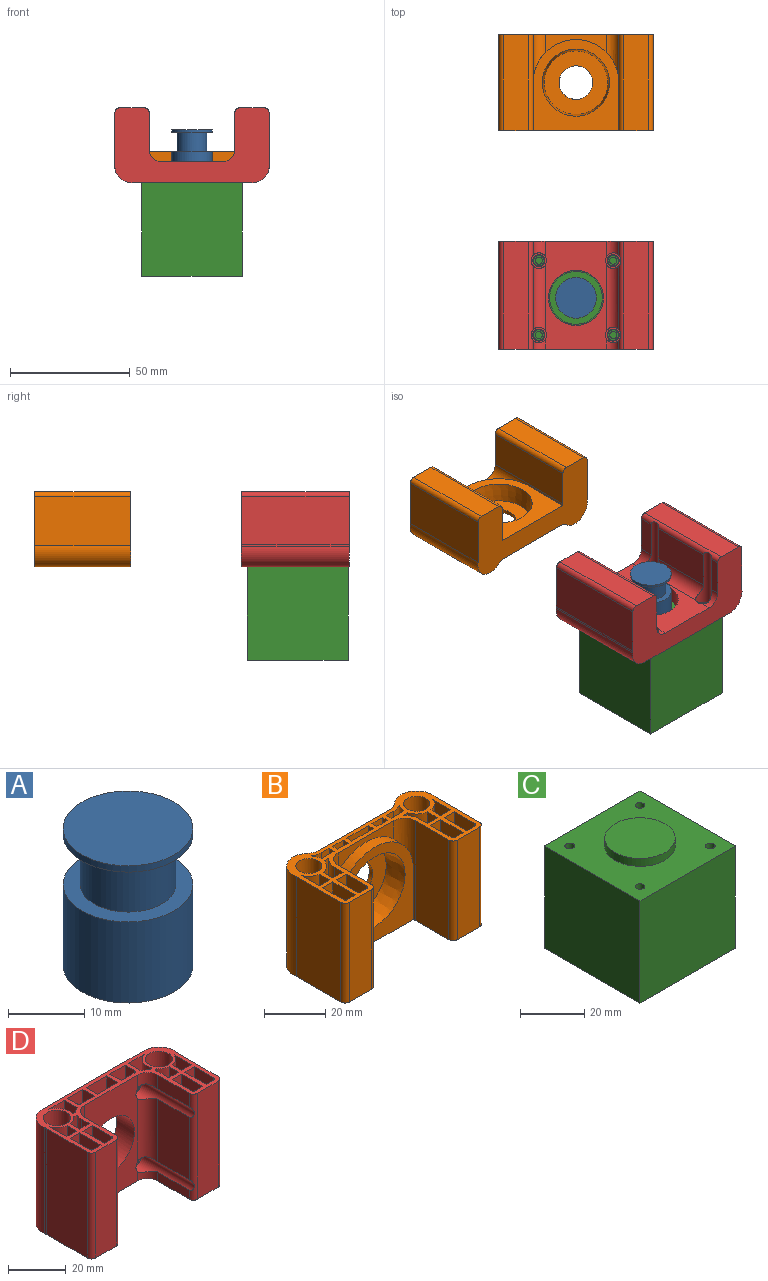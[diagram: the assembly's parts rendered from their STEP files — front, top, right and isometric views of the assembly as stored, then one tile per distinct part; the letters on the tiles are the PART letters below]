
ASSEMBLY  parts=4 mates=6
PART A: 7 faces, bbox 17x17x22 mm
  f0: cylinder r=6.25mm len=12.5mm, axis (0,0,1), area 314.2mm2, adj f3,f5
  f1: cylinder r=8.5mm len=17mm, axis (0,0,-1), area 694.3mm2, adj f2,f3
  f2: plane 17x17mm, normal (0,0,-1), area 227mm2, adj f1
  f3: plane 17x17mm, normal (0,0,1), area 104.3mm2, adj f0,f1
  f4: cylinder r=8.5mm len=17mm, axis (0,0,1), area 53.4mm2, adj f5,f6
  f5: plane 17x17mm, normal (0,0,-1), area 104.3mm2, adj f0,f4
  f6: plane 17x17mm, normal (0,0,1), area 227mm2, adj f4
PART B: 130 faces, bbox 64.5x31.3x40 mm
  f0: plane 10.18x2.3mm, normal (1,0,0), area 23.4mm2, adj f10,f16,f52,f109
  f1: plane 12.46x2.3mm, normal (-1,0,0), area 28.7mm2, adj f11,f52,f78,f106
  f2: plane 5.65x2.3mm, normal (1,0,0), area 13mm2, adj f9,f15,f52,f108
  f3: plane 6.31x2.3mm, normal (-1,0,0), area 14.5mm2, adj f10,f16,f52,f109
  f4: plane 5.65x2.3mm, normal (-1,0,0), area 13mm2, adj f9,f15,f52,f108
  f5: plane 6.31x2.3mm, normal (1,0,0), area 14.5mm2, adj f8,f14,f52,f107
  f6: plane 10.18x2.3mm, normal (-1,0,0), area 23.4mm2, adj f8,f14,f52,f107
  f7: plane 12.46x2.3mm, normal (1,0,0), area 28.7mm2, adj f52,f67,f88,f105
  f8: plane 10.18x5mm, normal (0,-1,0), area 39.8mm2, adj f5,f6,f52,f107
  f9: plane 10x5.65mm, normal (0,-1,0), area 50.8mm2, adj f2,f4,f52,f108
  f10: plane 10.18x5mm, normal (0,-1,0), area 39.8mm2, adj f0,f3,f52,f109
  f11: plane 38.4x3.49mm, normal (0,-1,0), area 113.6mm2, adj f1,f12,f52,f58,f69,f106
  f12: plane 10.86x2.3mm, normal (-1,0,0), area 25mm2, adj f11,f58,f78,f106
  f13: plane 10.86x2.3mm, normal (1,0,0), area 25mm2, adj f29,f67,f88,f105
  f14: plane 10.18x5mm, normal (0,1,0), area 39.8mm2, adj f5,f6,f52,f107
  f15: plane 10x5.65mm, normal (0,1,0), area 50.8mm2, adj f2,f4,f52,f108
  f16: plane 10.18x5mm, normal (0,1,0), area 39.8mm2, adj f0,f3,f52,f109
  f17: plane 8.85x6.3mm, normal (0,0,1), area 30.1mm2, adj f18,f25,f26,f89,f90,f94,f103
  f18: cylinder r=6.6mm len=38.4mm, axis (0,0,1), area 196.7mm2, adj f17,f26,f52,f89,f102,f103
  f19: cylinder r=5mm len=40mm, axis (0,0,-1), area 122.6mm2, adj f45,f46,f52,f53,f100,f101
  f20: cylinder r=5mm len=40mm, axis (0,0,1), area 122.6mm2, adj f46,f47,f52,f53,f100,f101
  f21: cylinder r=6.6mm len=38.4mm, axis (0,0,-1), area 196.7mm2, adj f31,f52,f63,f79,f98,f99
  f22: plane 8.36x4.7mm, normal (0,0,1), area 26.9mm2, adj f28,f30,f91,f93
  f23: plane 10.45x4.7mm, normal (0,0,1), area 48.9mm2, adj f65,f66,f77,f92,f97
  f24: plane 10.45x4.7mm, normal (0,0,1), area 48.9mm2, adj f27,f64,f76,f95,f96
  f25: cylinder r=5.85mm len=38.4mm, axis (0,0,-1), area 263.8mm2, adj f17,f52,f89,f90
  f26: plane 38.4x3.85mm, normal (1,0,0), area 147.8mm2, adj f17,f18,f52,f94
  f27: plane 38.4x3.7mm, normal (0,1,0), area 142.1mm2, adj f24,f52,f76,f96
  f28: plane 38.4x8.36mm, normal (-1,0,0), area 320.9mm2, adj f22,f30,f52,f93
  f29: plane 7.09x3.37mm, normal (0,0,1), area 15mm2, adj f13,f59,f67,f68,f88
  f30: cylinder r=5.85mm len=38.4mm, axis (0,0,-1), area 243.9mm2, adj f22,f28,f52,f91
  f31: plane 8.85x6.3mm, normal (0,0,1), area 30.1mm2, adj f21,f60,f63,f79,f81,f83,f98
  f32: plane 10.45x4.7mm, normal (0,0,1), area 48.9mm2, adj f37,f62,f75,f82,f87
  f33: plane 8.36x4.7mm, normal (0,0,1), area 26.9mm2, adj f34,f61,f80,f84
  f34: cylinder r=5.85mm len=38.4mm, axis (0,0,-1), area 243.9mm2, adj f33,f52,f61,f80
  f35: plane 38.4x9.45mm, normal (1,0,0), area 362.9mm2, adj f38,f52,f74,f85
  f36: plane 38.4x3.7mm, normal (0,1,0), area 142.1mm2, adj f38,f52,f74,f86
  f37: plane 38.4x9.45mm, normal (-1,0,0), area 362.9mm2, adj f32,f52,f75,f82
  f38: plane 10.45x4.7mm, normal (0,0,1), area 48.9mm2, adj f35,f36,f74,f85,f86
  f39: cylinder r=5.85mm len=38.4mm, axis (0,0,-1), area 138.7mm2, adj f52,f58,f69,f78
  f40: cylinder r=4.25mm len=38mm, axis (0,0,-1), area 1014.7mm2, adj f52,f55
  f41: cylinder r=4.25mm len=38mm, axis (0,0,-1), area 1014.7mm2, adj f52,f54
  f42: cylinder r=7.25mm len=40mm, axis (0,0,-1), area 730.8mm2, adj f43,f52,f53,f57
  f43: plane 40x20.53mm, normal (-1,0,0), area 821.3mm2, adj f42,f52,f53,f70
  f44: plane 40x10.2mm, normal (0,-1,0), area 408mm2, adj f52,f53,f70,f71
  f45: plane 40x15.5mm, normal (1,0,0), area 620mm2, adj f19,f52,f53,f71
  f46: plane 25.8x7.59mm, normal (0,-1,0), area 98.1mm2, adj f19,f20,f52,f101
  f47: plane 40x15.5mm, normal (-1,0,0), area 620mm2, adj f20,f52,f53,f72
  f48: plane 40x10.2mm, normal (0,-1,0), area 408mm2, adj f52,f53,f72,f73
  f49: plane 40x20.53mm, normal (1,0,0), area 821.3mm2, adj f50,f52,f53,f73
  f50: cylinder r=7.25mm len=40mm, axis (0,0,-1), area 730.8mm2, adj f49,f52,f53,f56
  f51: plane 40x33.38mm, normal (0,1,0), area 1181.2mm2, adj f52,f53,f56,f57,f110
  f52: plane 64.5x31.25mm, normal (0,0,1), area 554.8mm2, adj f0,f1,f2,f3,f4,f5,f6,f7
  f53: plane 64.5x31.25mm, normal (0,0,-1), area 1190.4mm2, adj f19,f20,f42,f43,f44,f45,f47,f48
  f54: plane 8.5x8.5mm, normal (0,0,1), area 56.7mm2, adj f41
  f55: plane 8.5x8.5mm, normal (0,0,1), area 56.7mm2, adj f40
  f56: cylinder r=5mm len=40mm, axis (0,0,-1), area 149.1mm2, adj f50,f51,f52,f53
  f57: cylinder r=5mm len=40mm, axis (0,0,-1), area 149.1mm2, adj f42,f51,f52,f53
  f58: plane 7.09x3.37mm, normal (0,0,1), area 15mm2, adj f11,f12,f39,f69,f78
  f59: cylinder r=5.85mm len=38.4mm, axis (0,0,-1), area 138.7mm2, adj f29,f52,f68,f88
  f60: cylinder r=5.85mm len=38.4mm, axis (0,0,-1), area 263.8mm2, adj f31,f52,f79,f81
  f61: plane 38.4x8.36mm, normal (1,0,0), area 320.9mm2, adj f33,f34,f52,f84
  f62: plane 38.4x3.7mm, normal (0,1,0), area 142.1mm2, adj f32,f52,f75,f87
  f63: plane 38.4x3.85mm, normal (-1,0,0), area 147.8mm2, adj f21,f31,f52,f83
  f64: plane 38.4x9.45mm, normal (1,0,0), area 362.9mm2, adj f24,f52,f76,f95
  f65: plane 38.4x3.7mm, normal (0,1,0), area 142.1mm2, adj f23,f52,f77,f97
  f66: plane 38.4x9.45mm, normal (-1,0,0), area 362.9mm2, adj f23,f52,f77,f92
  f67: plane 38.4x3.49mm, normal (0,-1,0), area 113.6mm2, adj f7,f13,f29,f52,f68,f105
  f68: cylinder r=6.6mm len=38.4mm, axis (0,0,-1), area 146.2mm2, adj f29,f52,f59,f67
  f69: cylinder r=6.6mm len=38.4mm, axis (0,0,-1), area 146.2mm2, adj f11,f39,f52,f58
  f70: cylinder r=2mm len=40mm, axis (0,0,-1), area 125.7mm2, adj f43,f44,f52,f53
  f71: cylinder r=2mm len=40mm, axis (0,0,1), area 125.7mm2, adj f44,f45,f52,f53
  f72: cylinder r=2mm len=40mm, axis (0,0,-1), area 125.7mm2, adj f47,f48,f52,f53
  f73: cylinder r=2mm len=40mm, axis (0,0,1), area 125.7mm2, adj f48,f49,f52,f53
  f74: cylinder r=1mm len=38.4mm, axis (0,0,1), area 60.3mm2, adj f35,f36,f38,f52
  f75: cylinder r=1mm len=38.4mm, axis (0,0,-1), area 60.3mm2, adj f32,f37,f52,f62
  f76: cylinder r=1mm len=38.4mm, axis (0,0,1), area 60.3mm2, adj f24,f27,f52,f64
  f77: cylinder r=1mm len=38.4mm, axis (0,0,-1), area 60.3mm2, adj f23,f52,f65,f66
  f78: plane 38.4x5.95mm, normal (0,1,0), area 208.1mm2, adj f1,f12,f39,f52,f58,f106
  f79: plane 38.4x2.14mm, normal (0,-1,0), area 67.1mm2, adj f21,f31,f52,f60,f98,f99
  f80: plane 38.4x4.56mm, normal (-1,0,0), area 174.9mm2, adj f33,f34,f52,f84
  f81: plane 38.4x4.56mm, normal (1,0,0), area 174.9mm2, adj f31,f52,f60,f83
  f82: plane 38.4x4.7mm, normal (0,-1,0), area 180.5mm2, adj f32,f37,f52,f87
  f83: plane 38.4x4.7mm, normal (0,1,0), area 180.5mm2, adj f31,f52,f63,f81
  f84: plane 38.4x4.7mm, normal (0,1,0), area 180.5mm2, adj f33,f52,f61,f80
  f85: plane 38.4x4.7mm, normal (0,-1,0), area 180.5mm2, adj f35,f38,f52,f86
  f86: plane 38.4x10.45mm, normal (-1,0,0), area 401.3mm2, adj f36,f38,f52,f85
  f87: plane 38.4x10.45mm, normal (1,0,0), area 401.3mm2, adj f32,f52,f62,f82
  f88: plane 38.4x5.95mm, normal (0,1,0), area 208.1mm2, adj f7,f13,f29,f52,f59,f105
  f89: plane 38.4x2.14mm, normal (0,-1,0), area 67.1mm2, adj f17,f18,f25,f52,f102,f103
  f90: plane 38.4x4.56mm, normal (-1,0,0), area 174.9mm2, adj f17,f25,f52,f94
  f91: plane 38.4x4.56mm, normal (1,0,0), area 174.9mm2, adj f22,f30,f52,f93
  f92: plane 38.4x4.7mm, normal (0,-1,0), area 180.5mm2, adj f23,f52,f66,f97
  f93: plane 38.4x4.7mm, normal (0,1,0), area 180.5mm2, adj f22,f28,f52,f91
  f94: plane 38.4x4.7mm, normal (0,1,0), area 180.5mm2, adj f17,f26,f52,f90
  f95: plane 38.4x4.7mm, normal (0,-1,0), area 180.5mm2, adj f24,f52,f64,f96
  f96: plane 38.4x10.45mm, normal (-1,0,0), area 401.3mm2, adj f24,f27,f52,f95
  f97: plane 38.4x10.45mm, normal (1,0,0), area 401.3mm2, adj f23,f52,f65,f92
  f98: plane 18.4x0.69mm, normal (-1,0,0), area 12.7mm2, adj f21,f31,f79,f99
  f99: cylinder r=17.9mm len=4.93mm, axis (0,1,0), area 2.2mm2, adj f21,f79,f98
  f100: plane 37.9x35.64mm, normal (0,-1,0), area 600.1mm2, adj f19,f20,f53,f101,f111
  f101: cylinder r=17.9mm len=35.64mm, axis (0,1,0), area 179.4mm2, adj f19,f20,f46,f100
  f102: cylinder r=17.9mm len=4.93mm, axis (0,1,0), area 2.2mm2, adj f18,f89,f103
  f103: plane 18.4x0.69mm, normal (1,0,0), area 12.7mm2, adj f17,f18,f89,f102
  f104: plane 26.5x26.5mm, normal (0,-1,0), area 397.6mm2, adj f110,f111
  f105: cylinder r=15.2mm len=15.07mm, axis (0,1,0), area 36.3mm2, adj f7,f13,f67,f88
  f106: cylinder r=15.2mm len=15.07mm, axis (0,1,0), area 36.3mm2, adj f1,f11,f12,f78
  f107: cylinder r=15.2mm len=5mm, axis (0,1,0), area 14.6mm2, adj f5,f6,f8,f14
  f108: cylinder r=15.2mm len=10mm, axis (0,1,0), area 23.4mm2, adj f2,f4,f9,f15
  f109: cylinder r=15.2mm len=5mm, axis (0,1,0), area 14.6mm2, adj f0,f3,f10,f16
  f110: cylinder r=7mm len=14mm, axis (0,-1,0), area 70.4mm2, adj f51,f104
  f111: cone r=13.25mm half-angle=5.4deg, axis (0,-1,0), area 687.9mm2, adj f100,f104
  f112: cylinder r=15.2mm len=5mm, axis (0,1,0), area 14.6mm2, adj f114,f115,f116,f117
  f113: plane 5x2.3mm, normal (0,0,1), area 11.5mm2, adj f114,f115,f116,f117
  f114: plane 4.71x2.3mm, normal (-1,0,0), area 10.8mm2, adj f112,f113,f116,f117
  f115: plane 8.58x2.3mm, normal (1,0,0), area 19.7mm2, adj f112,f113,f116,f117
  f116: plane 8.58x5mm, normal (0,1,0), area 31.8mm2, adj f112,f113,f114,f115
  f117: plane 8.58x5mm, normal (0,-1,0), area 31.8mm2, adj f112,f113,f114,f115
  f118: cylinder r=15.2mm len=10mm, axis (0,1,0), area 23.4mm2, adj f120,f121,f122,f123
  f119: plane 10x2.3mm, normal (0,0,1), area 23mm2, adj f120,f121,f122,f123
  f120: plane 4.05x2.3mm, normal (-1,0,0), area 9.3mm2, adj f118,f119,f122,f123
  f121: plane 4.05x2.3mm, normal (1,0,0), area 9.3mm2, adj f118,f119,f122,f123
  f122: plane 10x4.05mm, normal (0,1,0), area 34.8mm2, adj f118,f119,f120,f121
  f123: plane 10x4.05mm, normal (0,-1,0), area 34.8mm2, adj f118,f119,f120,f121
  f124: cylinder r=15.2mm len=5mm, axis (0,1,0), area 14.6mm2, adj f126,f127,f128,f129
  f125: plane 5x2.3mm, normal (0,0,1), area 11.5mm2, adj f126,f127,f128,f129
  f126: plane 8.58x2.3mm, normal (-1,0,0), area 19.7mm2, adj f124,f125,f128,f129
  f127: plane 4.71x2.3mm, normal (1,0,0), area 10.8mm2, adj f124,f125,f128,f129
  f128: plane 8.58x5mm, normal (0,1,0), area 31.8mm2, adj f124,f125,f126,f127
  f129: plane 8.58x5mm, normal (0,-1,0), area 31.8mm2, adj f124,f125,f126,f127
PART C: 16 faces, bbox 42x42x42 mm
  f0: plane 42x39mm, normal (0,-1,0), area 1638mm2, adj f1,f3,f4,f5
  f1: plane 42x39mm, normal (1,0,0), area 1638mm2, adj f0,f2,f4,f5
  f2: plane 42x39mm, normal (0,1,0), area 1638mm2, adj f1,f3,f4,f5
  f3: plane 42x39mm, normal (-1,0,0), area 1638mm2, adj f0,f2,f4,f5
  f4: plane 42x42mm, normal (0,0,1), area 1355.6mm2, adj f0,f1,f2,f3,f6,f8,f10,f12
  f5: plane 42x42mm, normal (0,0,-1), area 1764mm2, adj f0,f1,f2,f3
  f6: cylinder r=11mm len=22mm, axis (0,0,-1), area 207.3mm2, adj f4,f7
  f7: plane 22x22mm, normal (0,0,1), area 380.1mm2, adj f6
  f8: cylinder r=1.5mm len=5mm, axis (0,0,1), area 47.1mm2, adj f4,f9
  f9: plane 3x3mm, normal (0,0,1), area 7.1mm2, adj f8
  f10: cylinder r=1.5mm len=5mm, axis (0,0,1), area 47.1mm2, adj f4,f11
  f11: plane 3x3mm, normal (0,0,1), area 7.1mm2, adj f10
  f12: cylinder r=1.5mm len=5mm, axis (0,0,1), area 47.1mm2, adj f4,f13
  f13: plane 3x3mm, normal (0,0,1), area 7.1mm2, adj f12
  f14: cylinder r=1.5mm len=5mm, axis (0,0,1), area 47.1mm2, adj f4,f15
  f15: plane 3x3mm, normal (0,0,1), area 7.1mm2, adj f14
PART D: 206 faces, bbox 64.5x31.3x45 mm
  f0: plane 5x5mm, normal (0,-1,0), area 4.4mm2, adj f159,f199
  f1: cylinder r=3.25mm len=25.89mm, axis (0,1,0), area 194.1mm2, adj f17,f18,f19,f20,f77,f80,f198
  f2: plane 5x5mm, normal (0,-1,0), area 4.4mm2, adj f156,f197
  f3: cylinder r=3.25mm len=25.89mm, axis (0,1,0), area 194.1mm2, adj f18,f20,f77,f78,f79,f80,f196
  f4: plane 5x5mm, normal (0,-1,0), area 4.4mm2, adj f162,f195
  f5: cylinder r=3.25mm len=25.89mm, axis (0,1,0), area 194.1mm2, adj f13,f14,f15,f74,f76,f77,f194
  f6: plane 5x5mm, normal (0,-1,0), area 4.4mm2, adj f153,f193
  f7: cylinder r=3.25mm len=25.89mm, axis (0,1,0), area 194.1mm2, adj f14,f15,f16,f74,f75,f77,f192
  f8: cylinder r=11.5mm len=23mm, axis (0,1,0), area 632.2mm2, adj f69,f77
  f9: plane 13.48x1.22mm, normal (-0.47,0.88,0), area 16.6mm2, adj f27,f46,f58,f190
  f10: plane 13.48x1.22mm, normal (0.47,0.88,0), area 16.6mm2, adj f24,f50,f53,f184
  f11: cylinder r=2mm len=7.37mm, axis (0,0,1), area 12.3mm2, adj f49,f53,f55,f176
  f12: cylinder r=2mm len=7.37mm, axis (0,0,1), area 12.3mm2, adj f28,f49,f58,f168
  f13: plane 15.5x3.81mm, normal (-1,0,0), area 59mm2, adj f5,f70,f74,f76
  f14: plane 26.62x15.5mm, normal (-1,0,0), area 412.6mm2, adj f5,f7,f15,f74
  f15: cylinder r=5mm len=27.1mm, axis (0,0,1), area 199.8mm2, adj f5,f7,f14,f77
  f16: cylinder r=5mm len=6.05mm, axis (0,0,1), area 41mm2, adj f7,f49,f75,f77
  f17: cylinder r=5mm len=5mm, axis (0,0,-1), area 25.3mm2, adj f1,f19,f70,f77
  f18: cylinder r=5mm len=27.1mm, axis (0,0,-1), area 199.8mm2, adj f1,f3,f20,f77
  f19: plane 15.5x3.81mm, normal (1,0,0), area 59mm2, adj f1,f17,f70,f80
  f20: plane 26.62x15.5mm, normal (1,0,0), area 412.6mm2, adj f1,f3,f18,f80
  f21: plane 6.17x1.41mm, normal (-1,0,0), area 3.7mm2, adj f23,f51,f56,f161,f184,f185
  f22: plane 25.01x6.17mm, normal (-1,0,0), area 144.4mm2, adj f24,f56,f158,f161,f176,f177,f184,f185
  f23: cylinder r=6.6mm len=2.59mm, axis (0,0,-1), area 2.6mm2, adj f21,f51,f54,f184
  f24: cylinder r=6.6mm len=24.47mm, axis (0,0,-1), area 61.8mm2, adj f10,f22,f50,f147,f176,f184
  f25: plane 6.17x1.41mm, normal (1,0,0), area 3.7mm2, adj f57,f60,f62,f164,f190,f191
  f26: plane 25.01x6.17mm, normal (1,0,0), area 144.4mm2, adj f27,f60,f154,f164,f168,f169,f190,f191
  f27: cylinder r=6.6mm len=24.47mm, axis (0,0,1), area 61.8mm2, adj f9,f26,f46,f148,f168,f190
  f28: cylinder r=6.6mm len=4.4mm, axis (0,0,1), area 8.4mm2, adj f12,f49,f61,f168
  f29: plane 4.55x1.75mm, normal (1,0,0), area 4.3mm2, adj f42,f101,f105,f160,f182,f183
  f30: plane 25.69x4.55mm, normal (1,0,0), area 109.7mm2, adj f43,f105,f157,f160,f174,f175,f182,f183
  f31: cylinder r=6.6mm len=1.29mm, axis (0,0,-1), area 0.2mm2, adj f42,f101,f106,f182
  f32: cylinder r=6.6mm len=24.79mm, axis (0,0,-1), area 4.3mm2, adj f43,f106,f174,f182
  f33: plane 9.52x5.55mm, normal (-1,0,0), area 52.8mm2, adj f101,f105,f106,f167
  f34: plane 12.26x10mm, normal (0,1,0), area 115.5mm2, adj f49,f107,f108,f166
  f35: plane 9.52x5.55mm, normal (1,0,0), area 52.8mm2, adj f110,f112,f115,f165
  f36: plane 4.55x1.75mm, normal (-1,0,0), area 4.3mm2, adj f110,f115,f149,f163,f186,f187
  f37: plane 25.69x4.55mm, normal (-1,0,0), area 109.7mm2, adj f40,f115,f155,f163,f172,f173,f186,f187
  f38: cylinder r=6.6mm len=24.79mm, axis (0,0,1), area 4.3mm2, adj f40,f112,f173,f186
  f39: cylinder r=6.6mm len=4.89mm, axis (0,0,1), area 0.8mm2, adj f41,f49,f112,f173
  f40: cylinder r=1mm len=24.51mm, axis (0,0,1), area 37.9mm2, adj f37,f38,f173,f186
  f41: cylinder r=1mm len=4.76mm, axis (0,0,1), area 7mm2, adj f39,f49,f113,f173
  f42: cylinder r=1mm len=1.16mm, axis (0,0,-1), area 1.2mm2, adj f29,f31,f101,f182
  f43: cylinder r=1mm len=24.51mm, axis (0,0,-1), area 37.9mm2, adj f30,f32,f174,f182
  f44: cylinder r=4.25mm len=17.5mm, axis (0,0,-1), area 467.3mm2, adj f45,f152
  f45: plane 8.5x8.5mm, normal (0,0,1), area 56.7mm2, adj f44
  f46: plane 2.16x1.06mm, normal (0,0,-1), area 0.5mm2, adj f9,f27,f58,f148
  f47: cylinder r=4.7mm len=25.05mm, axis (0,0,-1), area 739.8mm2, adj f49,f152
  f48: cylinder r=4.7mm len=25.05mm, axis (0,0,-1), area 739.8mm2, adj f49,f151
  f49: plane 64.5x31.25mm, normal (0,0,1), area 545.3mm2, adj f11,f12,f16,f28,f34,f39,f41,f47
  f50: plane 2.16x1.06mm, normal (0,0,-1), area 0.5mm2, adj f10,f24,f53,f147
  f51: plane 8.35x7.78mm, normal (0,0,1), area 31.9mm2, adj f21,f23,f53,f54,f56
  f52: plane 6.17x5.01mm, normal (-1,0,0), area 25.9mm2, adj f49,f55,f56,f158,f176,f177
  f53: cylinder r=5.85mm len=43.4mm, axis (0,0,-1), area 397.5mm2, adj f10,f11,f49,f50,f51,f54,f56,f147
  f54: plane 3.88x1.22mm, normal (0.47,0.88,0), area 3.2mm2, adj f23,f51,f53,f184
  f55: cylinder r=6.6mm len=4.4mm, axis (0,0,-1), area 8.4mm2, adj f11,f49,f52,f176
  f56: plane 43.4x7.78mm, normal (0,-1,0), area 311.9mm2, adj f21,f22,f49,f51,f52,f53,f158,f161
  f57: plane 8.35x7.78mm, normal (0,0,1), area 31.9mm2, adj f25,f58,f59,f60,f62
  f58: cylinder r=5.85mm len=43.4mm, axis (0,0,-1), area 397.4mm2, adj f9,f12,f46,f49,f57,f59,f60,f148
  f59: plane 3.88x1.22mm, normal (-0.47,0.88,0), area 3.2mm2, adj f57,f58,f62,f190
  f60: plane 43.4x7.78mm, normal (0,-1,0), area 311.9mm2, adj f25,f26,f49,f57,f58,f61,f154,f164
  f61: plane 6.17x5.01mm, normal (1,0,0), area 25.9mm2, adj f28,f49,f60,f154,f168,f169
  f62: cylinder r=6.6mm len=2.59mm, axis (0,0,1), area 2.6mm2, adj f25,f57,f59,f190
  f63: plane 8.5x8.5mm, normal (0,0,1), area 56.7mm2, adj f64
  f64: cylinder r=4.25mm len=17.5mm, axis (0,0,-1), area 467.3mm2, adj f63,f151
  f65: cylinder r=5mm len=45mm, axis (0,0,-1), area 35.2mm2, adj f49,f67,f70,f71
  f66: cylinder r=5mm len=45mm, axis (0,0,-1), area 35.2mm2, adj f49,f68,f70,f82
  f67: cylinder r=7.25mm len=45mm, axis (0,0,-1), area 563.6mm2, adj f49,f65,f69,f70
  f68: cylinder r=7.25mm len=45mm, axis (0,0,-1), area 563.6mm2, adj f49,f66,f69,f70
  f69: plane 50x45mm, normal (0,1,0), area 1773.7mm2, adj f8,f49,f67,f68,f70,f153,f156,f159
  f70: plane 64.5x31.25mm, normal (0,0,-1), area 1188mm2, adj f13,f17,f19,f65,f66,f67,f68,f69
  f71: plane 45x20.09mm, normal (1,0,0), area 904mm2, adj f49,f65,f70,f72
  f72: cylinder r=2mm len=45mm, axis (0,0,1), area 141.4mm2, adj f49,f70,f71,f73
  f73: plane 45x10.2mm, normal (0,-1,0), area 459mm2, adj f49,f70,f72,f74
  f74: cylinder r=2mm len=45mm, axis (0,0,-1), area 128.1mm2, adj f5,f7,f13,f14,f49,f70,f73,f75
  f75: plane 15.5x5.81mm, normal (-1,0,0), area 90mm2, adj f7,f16,f49,f74
  f76: cylinder r=5mm len=5mm, axis (0,0,1), area 25.3mm2, adj f5,f13,f70,f77
  f77: plane 45x25.8mm, normal (0,-1,0), area 738.6mm2, adj f1,f3,f5,f7,f8,f15,f16,f17
  f78: cylinder r=5mm len=6.05mm, axis (0,0,-1), area 41mm2, adj f3,f49,f77,f79
  f79: plane 15.5x5.81mm, normal (1,0,0), area 90mm2, adj f3,f49,f78,f80
  f80: cylinder r=2mm len=45mm, axis (0,0,1), area 128.1mm2, adj f1,f3,f19,f20,f49,f70,f79,f81
  f81: plane 45x10.2mm, normal (0,-1,0), area 459mm2, adj f49,f70,f80,f83
  f82: plane 45x20.09mm, normal (-1,0,0), area 904mm2, adj f49,f66,f70,f83
  f83: cylinder r=2mm len=45mm, axis (0,0,-1), area 141.4mm2, adj f49,f70,f81,f82
  f84: plane 8.36x4.7mm, normal (0,0,1), area 26.9mm2, adj f85,f86,f87,f88
  f85: plane 43.4x8.36mm, normal (1,0,0), area 362.7mm2, adj f49,f84,f86,f88
  f86: plane 43.4x4.7mm, normal (0,1,0), area 204mm2, adj f49,f84,f85,f87
  f87: plane 43.4x4.56mm, normal (-1,0,0), area 197.7mm2, adj f49,f84,f86,f88
  f88: cylinder r=5.85mm len=43.4mm, axis (0,0,-1), area 275.7mm2, adj f49,f84,f85,f87
  f89: plane 10.45x4.7mm, normal (0,0,1), area 48.9mm2, adj f90,f91,f92,f93,f94
  f90: cylinder r=1mm len=43.4mm, axis (0,0,1), area 68.2mm2, adj f49,f89,f93,f94
  f91: plane 43.4x4.7mm, normal (0,-1,0), area 204mm2, adj f49,f89,f92,f94
  f92: plane 43.4x10.45mm, normal (-1,0,0), area 453.5mm2, adj f49,f89,f91,f93
  f93: plane 43.4x3.7mm, normal (0,1,0), area 160.6mm2, adj f49,f89,f90,f92
  f94: plane 43.4x9.45mm, normal (1,0,0), area 410.1mm2, adj f49,f89,f90,f91
  f95: plane 10.45x4.7mm, normal (0,0,1), area 48.9mm2, adj f96,f97,f98,f99,f100
  f96: cylinder r=1mm len=43.4mm, axis (0,0,-1), area 68.2mm2, adj f49,f95,f99,f100
  f97: plane 43.4x4.7mm, normal (0,-1,0), area 204mm2, adj f49,f95,f98,f100
  f98: plane 43.4x10.45mm, normal (1,0,0), area 453.5mm2, adj f49,f95,f97,f99
  f99: plane 43.4x3.7mm, normal (0,1,0), area 160.6mm2, adj f49,f95,f96,f98
  f100: plane 43.4x9.45mm, normal (-1,0,0), area 410.1mm2, adj f49,f95,f96,f97
  f101: plane 7.5x5.55mm, normal (0,0,1), area 41.4mm2, adj f29,f31,f33,f42,f105,f106
  f102: plane 5.35x4.55mm, normal (1,0,0), area 20.7mm2, adj f49,f105,f150,f157,f174,f175
  f103: cylinder r=6.6mm len=4.89mm, axis (0,0,-1), area 0.8mm2, adj f49,f106,f150,f174
  f104: plane 13.12x5.55mm, normal (-1,0,0), area 72.8mm2, adj f49,f105,f106,f167
  f105: plane 43.4x7.5mm, normal (0,-1,0), area 229.9mm2, adj f29,f30,f33,f49,f101,f102,f104,f157
  f106: plane 43.4x6.3mm, normal (0,1,0), area 177.5mm2, adj f31,f32,f33,f49,f101,f103,f104,f167
  f107: plane 12.26x5.55mm, normal (1,0,0), area 68.1mm2, adj f34,f49,f109,f166
  f108: plane 12.26x5.55mm, normal (-1,0,0), area 68.1mm2, adj f34,f49,f109,f166
  f109: plane 12.26x10mm, normal (0,-1,0), area 115.5mm2, adj f49,f107,f108,f166
  f110: plane 7.5x5.55mm, normal (0,0,1), area 41.4mm2, adj f35,f36,f112,f114,f115,f149
  f111: plane 13.12x5.55mm, normal (1,0,0), area 72.8mm2, adj f49,f112,f115,f165
  f112: plane 43.4x6.3mm, normal (0,1,0), area 177.5mm2, adj f35,f38,f39,f49,f110,f111,f114,f165
  f113: plane 5.35x4.55mm, normal (-1,0,0), area 20.7mm2, adj f41,f49,f115,f155,f172,f173
  f114: cylinder r=6.6mm len=1.29mm, axis (0,0,1), area 0.2mm2, adj f110,f112,f149,f186
  f115: plane 43.4x7.5mm, normal (0,-1,0), area 229.9mm2, adj f35,f36,f37,f49,f110,f111,f113,f155
  f116: plane 10.45x4.7mm, normal (0,0,1), area 48.9mm2, adj f117,f118,f119,f120,f121
  f117: plane 43.4x4.7mm, normal (0,-1,0), area 204mm2, adj f49,f116,f118,f120
  f118: plane 43.4x9.45mm, normal (1,0,0), area 410.1mm2, adj f49,f116,f117,f119
  f119: cylinder r=1mm len=43.4mm, axis (0,0,1), area 68.2mm2, adj f49,f116,f118,f121
  f120: plane 43.4x10.45mm, normal (-1,0,0), area 453.5mm2, adj f49,f116,f117,f121
  f121: plane 43.4x3.7mm, normal (0,1,0), area 160.6mm2, adj f49,f116,f119,f120
  f122: plane 8.36x4.7mm, normal (0,0,1), area 26.9mm2, adj f123,f124,f125,f126
  f123: plane 43.4x4.7mm, normal (0,1,0), area 204mm2, adj f49,f122,f125,f126
  f124: cylinder r=5.85mm len=43.4mm, axis (0,0,-1), area 275.7mm2, adj f49,f122,f125,f126
  f125: plane 43.4x4.56mm, normal (1,0,0), area 197.7mm2, adj f49,f122,f123,f124
  f126: plane 43.4x8.36mm, normal (-1,0,0), area 362.7mm2, adj f49,f122,f123,f124
  f127: plane 10.45x4.7mm, normal (0,0,1), area 48.9mm2, adj f128,f129,f130,f131,f132
  f128: cylinder r=1mm len=43.4mm, axis (0,0,-1), area 68.2mm2, adj f49,f127,f129,f132
  f129: plane 43.4x9.45mm, normal (-1,0,0), area 410.1mm2, adj f49,f127,f128,f130
  f130: plane 43.4x4.7mm, normal (0,-1,0), area 204mm2, adj f49,f127,f129,f131
  f131: plane 43.4x10.45mm, normal (1,0,0), area 453.5mm2, adj f49,f127,f130,f132
  f132: plane 43.4x3.7mm, normal (0,1,0), area 160.6mm2, adj f49,f127,f128,f131
  f133: plane 6.9x5.15mm, normal (0,0,1), area 26.6mm2, adj f134,f135,f136,f137,f138,f139
  f134: plane 43.4x4.56mm, normal (1,0,0), area 197.7mm2, adj f49,f133,f135,f138
  f135: plane 43.4x4.7mm, normal (0,1,0), area 204mm2, adj f49,f133,f134,f136
  f136: plane 43.4x3.85mm, normal (-1,0,0), area 167.1mm2, adj f49,f133,f135,f139
  f137: plane 43.4x1.22mm, normal (-0.47,-0.88,0), area 57.3mm2, adj f49,f133,f138,f139,f179,f181
  f138: cylinder r=5.85mm len=43.4mm, axis (0,0,-1), area 204mm2, adj f49,f133,f134,f137
  f139: cylinder r=6.6mm len=43.4mm, axis (0,0,-1), area 94.9mm2, adj f49,f133,f136,f137,f178,f179,f180,f181
  f140: plane 6.9x5.15mm, normal (0,0,1), area 26.6mm2, adj f141,f142,f143,f144,f145,f146
  f141: cylinder r=6.6mm len=43.4mm, axis (0,0,1), area 94.9mm2, adj f49,f140,f142,f145,f170,f171,f188,f189
  f142: plane 43.4x1.22mm, normal (0.47,-0.88,0), area 57.3mm2, adj f49,f140,f141,f146,f170,f188
  f143: plane 43.4x4.7mm, normal (0,1,0), area 204mm2, adj f49,f140,f144,f145
  f144: plane 43.4x4.56mm, normal (-1,0,0), area 197.7mm2, adj f49,f140,f143,f146
  f145: plane 43.4x3.85mm, normal (1,0,0), area 167.1mm2, adj f49,f140,f141,f143
  f146: cylinder r=5.85mm len=43.4mm, axis (0,0,-1), area 204mm2, adj f49,f140,f142,f144
  f147: cylinder r=2mm len=16.37mm, axis (0,0,1), area 33mm2, adj f24,f50,f53,f176
  f148: cylinder r=2mm len=16.37mm, axis (0,0,1), area 33mm2, adj f27,f46,f58,f168
  f149: cylinder r=1mm len=1.16mm, axis (0,0,1), area 1.2mm2, adj f36,f110,f114,f186
  f150: cylinder r=1mm len=4.76mm, axis (0,0,-1), area 7mm2, adj f49,f102,f103,f174
  f151: cone r=4.25mm half-angle=45deg, axis (0,0,1), area 17.9mm2, adj f48,f64
  f152: cone r=4.25mm half-angle=45deg, axis (0,0,1), area 17.9mm2, adj f44,f47
  f153: cylinder r=2.2mm len=4.4mm, axis (0,1,0), area 41.5mm2, adj f6,f69
  f154: cylinder r=3mm len=5.99mm, axis (0,1,0), area 12.6mm2, adj f26,f60,f61,f169
  f155: cylinder r=3mm len=5.31mm, axis (0,1,0), area 9.1mm2, adj f37,f113,f115,f172
  f156: cylinder r=2.2mm len=4.4mm, axis (0,1,0), area 41.5mm2, adj f2,f69
  f157: cylinder r=3mm len=5.31mm, axis (0,1,0), area 9.1mm2, adj f30,f102,f105,f175
  f158: cylinder r=3mm len=5.99mm, axis (0,1,0), area 12.6mm2, adj f22,f52,f56,f177
  f159: cylinder r=2.2mm len=4.4mm, axis (0,1,0), area 41.5mm2, adj f0,f69
  f160: cylinder r=3mm len=5.31mm, axis (0,1,0), area 9.1mm2, adj f29,f30,f105,f183
  f161: cylinder r=3mm len=5.99mm, axis (0,1,0), area 12.6mm2, adj f21,f22,f56,f185
  f162: cylinder r=2.2mm len=4.4mm, axis (0,1,0), area 41.5mm2, adj f4,f69
  f163: cylinder r=3mm len=5.31mm, axis (0,1,0), area 9.1mm2, adj f36,f37,f115,f187
  f164: cylinder r=3mm len=5.99mm, axis (0,1,0), area 12.6mm2, adj f25,f26,f60,f191
  f165: cylinder r=12.3mm len=20.76mm, axis (0,1,0), area 137.1mm2, adj f35,f111,f112,f115
  f166: cylinder r=12.3mm len=10mm, axis (0,1,0), area 57.2mm2, adj f34,f107,f108,f109
  f167: cylinder r=12.3mm len=20.76mm, axis (0,1,0), area 137.1mm2, adj f33,f104,f105,f106
  f168: cylinder r=4.05mm len=8.09mm, axis (0,1,0), area 62.1mm2, adj f12,f26,f27,f28,f58,f61,f148,f169
  f169: plane 8.09x3.85mm, normal (0,1,0), area 11.2mm2, adj f26,f61,f154,f168
  f170: cylinder r=4.05mm len=3.9mm, axis (0,1,0), area 6.4mm2, adj f141,f142,f171
  f171: plane 1.27x0.05mm, normal (0,-1,0), area 0mm2, adj f141,f170
  f172: plane 7.6x2.65mm, normal (0,1,0), area 8.6mm2, adj f37,f113,f155,f173
  f173: cylinder r=4.05mm len=7.6mm, axis (0,1,0), area 40.5mm2, adj f37,f38,f39,f40,f41,f112,f113,f172
  f174: cylinder r=4.05mm len=7.6mm, axis (0,1,0), area 40.5mm2, adj f30,f32,f43,f102,f103,f106,f150,f175
  f175: plane 7.6x2.65mm, normal (0,1,0), area 8.6mm2, adj f30,f102,f157,f174
  f176: cylinder r=4.05mm len=8.09mm, axis (0,1,0), area 62.1mm2, adj f11,f22,f24,f52,f53,f55,f147,f177
  f177: plane 8.09x3.85mm, normal (0,1,0), area 11.2mm2, adj f22,f52,f158,f176
  f178: plane 1.27x0.05mm, normal (0,-1,0), area 0mm2, adj f139,f179
  f179: cylinder r=4.05mm len=3.9mm, axis (0,1,0), area 6.4mm2, adj f137,f139,f178
  f180: plane 1.27x0.05mm, normal (0,-1,0), area 0mm2, adj f139,f181
  f181: cylinder r=4.05mm len=3.9mm, axis (0,1,0), area 6.4mm2, adj f137,f139,f180
  f182: cylinder r=4.05mm len=7.6mm, axis (0,1,0), area 40.5mm2, adj f29,f30,f31,f32,f42,f43,f106,f183
  f183: plane 7.6x2.65mm, normal (0,1,0), area 8.6mm2, adj f29,f30,f160,f182
  f184: cylinder r=4.05mm len=8.09mm, axis (0,1,0), area 63.5mm2, adj f10,f21,f22,f23,f24,f53,f54,f185
  f185: plane 8.09x3.85mm, normal (0,1,0), area 11.2mm2, adj f21,f22,f161,f184
  f186: cylinder r=4.05mm len=7.6mm, axis (0,1,0), area 40.5mm2, adj f36,f37,f38,f40,f112,f114,f149,f187
  f187: plane 7.6x2.65mm, normal (0,1,0), area 8.6mm2, adj f36,f37,f163,f186
  f188: cylinder r=4.05mm len=3.9mm, axis (0,1,0), area 6.4mm2, adj f141,f142,f189
  f189: plane 1.27x0.05mm, normal (0,-1,0), area 0mm2, adj f141,f188
  f190: cylinder r=4.05mm len=8.09mm, axis (0,1,0), area 63.5mm2, adj f9,f25,f26,f27,f58,f59,f62,f191
  f191: plane 8.09x3.85mm, normal (0,1,0), area 11.2mm2, adj f25,f26,f164,f190
  f192: plane 6.5x6.5mm, normal (0,-1,0), area 13.5mm2, adj f7,f193
  f193: cylinder r=2.5mm len=5mm, axis (0,1,0), area 31.4mm2, adj f6,f192
  f194: plane 6.5x6.5mm, normal (0,-1,0), area 13.5mm2, adj f5,f195
  f195: cylinder r=2.5mm len=5mm, axis (0,1,0), area 31.4mm2, adj f4,f194
  f196: plane 6.5x6.5mm, normal (0,-1,0), area 13.5mm2, adj f3,f197
  f197: cylinder r=2.5mm len=5mm, axis (0,1,0), area 31.4mm2, adj f2,f196
  f198: plane 6.5x6.5mm, normal (0,-1,0), area 13.5mm2, adj f1,f199
  f199: cylinder r=2.5mm len=5mm, axis (0,1,0), area 31.4mm2, adj f0,f198
  f200: cylinder r=12.3mm len=10mm, axis (0,1,0), area 57.2mm2, adj f202,f203,f204,f205
  f201: plane 10x5.55mm, normal (0,0,1), area 55.5mm2, adj f202,f203,f204,f205
  f202: plane 8.66x5.55mm, normal (1,0,0), area 48.1mm2, adj f200,f201,f204,f205
  f203: plane 8.66x5.55mm, normal (-1,0,0), area 48.1mm2, adj f200,f201,f204,f205
  f204: plane 10x8.66mm, normal (0,1,0), area 79.5mm2, adj f200,f201,f202,f203
  f205: plane 10x8.66mm, normal (0,-1,0), area 79.5mm2, adj f200,f201,f202,f203
PLACE A rot(axis=(0,0,-1),90deg) t=(4.74,-0.77,-136.79)mm
PLACE B rot(axis=(-1,0,0),90deg) t=(4.74,68.92,-87.54)mm
PLACE C t=(4.74,-0.77,-133.79)mm
PLACE D rot(axis=(-1,0,0),90deg) t=(4.74,-22.27,-87.54)mm
MATE cylindrical A.f0 <-> C.f6  axis (0,0,-1) through (4.74,-0.77,-88.29)mm
MATE planar A.f0 <-> C.f6  axis (0,0,-1) through (4.74,-0.77,-94.79)mm
MATE planar B.f43 <-> D.f82  axis (-1,0,0) through (-27.36,88.92,-75.8)mm
MATE planar D.f69 <-> C.f6  axis (0,0,-1) through (4.74,0.5,-94.79)mm
MATE planar B.f44 <-> D.f81  axis (0,0,1) through (-20.26,88.92,-63.54)mm
MATE cylindrical D.f1 <-> C.f14  axis (0,0,-1) through (-10.76,-16.27,-93.29)mm
